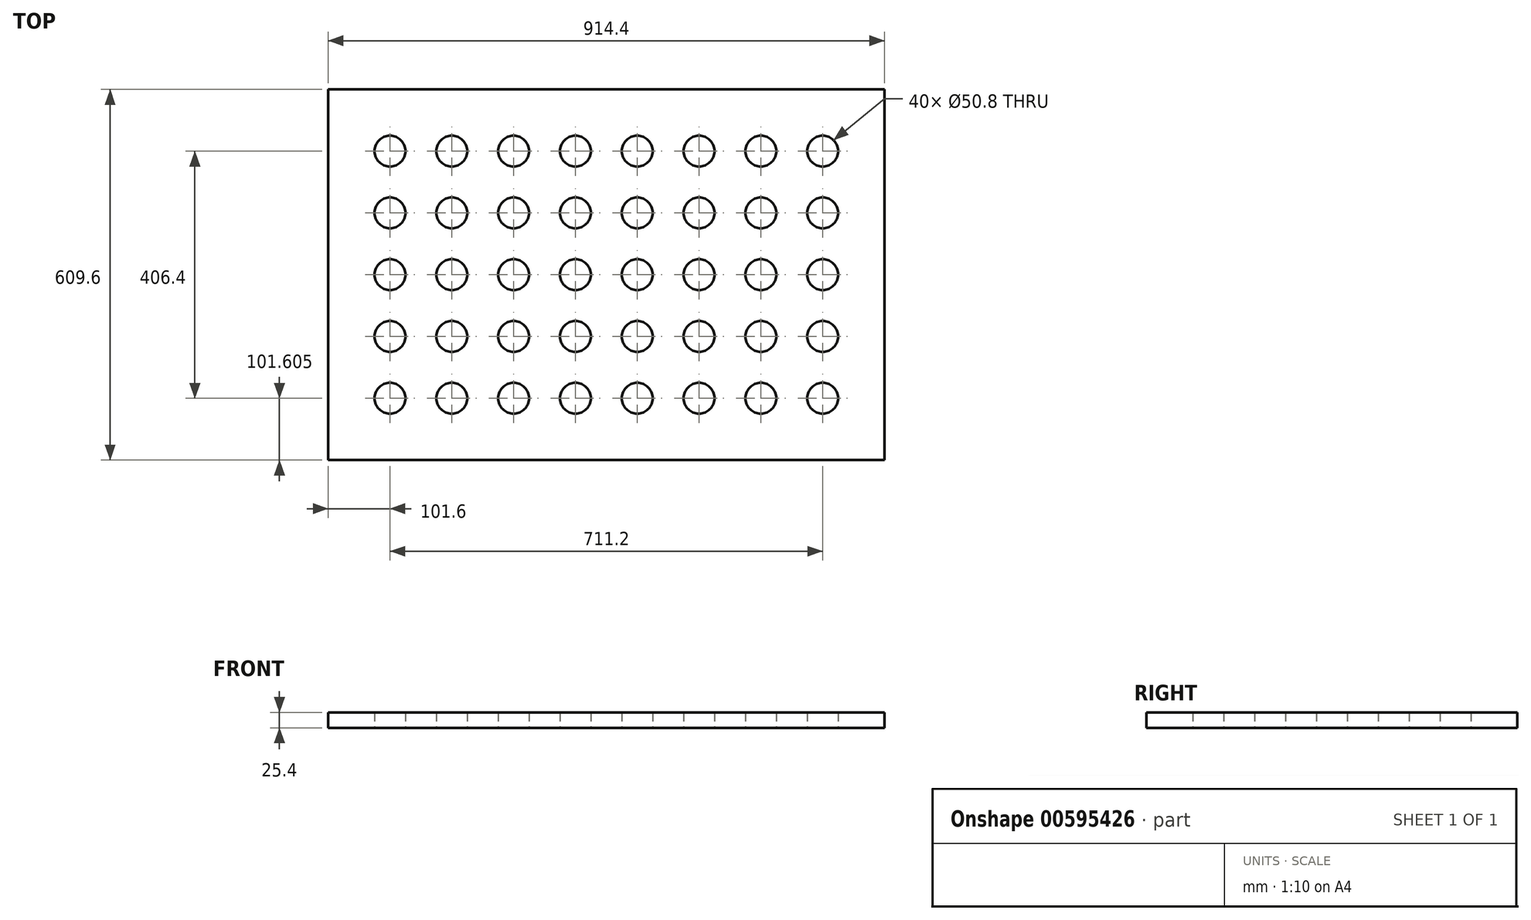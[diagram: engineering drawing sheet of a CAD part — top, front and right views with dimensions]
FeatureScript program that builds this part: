
annotation { "Feature Type Name" : "Feature", "Feature Type Description" : "" }
export const myFeature = defineFeature(function(context is Context, id is Id, definition is map)
    precondition{}
    {
        {
            var Q0;
            Q0=qCreatedBy(makeId("Top.planeOp"),FACE);
            var sketch = newSketch(context, id + "F0", { "sketchPlane" : qUnion([Q0])});
            skLineSegment(sketch, "E0.bottom", {"start": v(812.8, 482.96) * mm, "end": v(-101.6, 482.96) * mm});
            skLineSegment(sketch, "E0.top", {"start": v(812.8, -126.64) * mm, "end": v(-101.6, -126.64) * mm});
            skLineSegment(sketch, "E0.left", {"start": v(812.8, 482.96) * mm, "end": v(812.8, -126.64) * mm});
            skLineSegment(sketch, "E0.right", {"start": v(-101.6, 482.96) * mm, "end": v(-101.6, -126.64) * mm});
            skCircle(sketch, "E1", {"center": v(0, 381.36) * mm, "radius": 25.4 * mm});
            skCircle(sketch, "E2", {"center": v(101.6, 381.36) * mm, "radius": 25.4 * mm});
            skCircle(sketch, "E3", {"center": v(203.2, 381.36) * mm, "radius": 25.4 * mm});
            skCircle(sketch, "E4", {"center": v(304.8, 381.36) * mm, "radius": 25.4 * mm});
            skCircle(sketch, "E5", {"center": v(406.4, 381.36) * mm, "radius": 25.4 * mm});
            skCircle(sketch, "E6", {"center": v(508, 381.36) * mm, "radius": 25.4 * mm});
            skCircle(sketch, "E7", {"center": v(609.6, 381.36) * mm, "radius": 25.4 * mm});
            skCircle(sketch, "E8", {"center": v(711.2, 381.36) * mm, "radius": 25.4 * mm});
            skCircle(sketch, "E9", {"center": v(0, 279.76) * mm, "radius": 25.4 * mm});
            skCircle(sketch, "E10", {"center": v(0, 178.16) * mm, "radius": 25.4 * mm});
            skCircle(sketch, "E11", {"center": v(0, 76.56) * mm, "radius": 25.4 * mm});
            skCircle(sketch, "E12", {"center": v(0, -25.04) * mm, "radius": 25.4 * mm});
            skCircle(sketch, "E13", {"center": v(101.6, 279.76) * mm, "radius": 25.4 * mm});
            skCircle(sketch, "E14", {"center": v(101.6, 178.16) * mm, "radius": 25.4 * mm});
            skCircle(sketch, "E15", {"center": v(101.6, 76.56) * mm, "radius": 25.4 * mm});
            skCircle(sketch, "E16", {"center": v(101.6, -25.04) * mm, "radius": 25.4 * mm});
            skCircle(sketch, "E17", {"center": v(203.2, 279.76) * mm, "radius": 25.4 * mm});
            skCircle(sketch, "E18", {"center": v(304.8, 279.76) * mm, "radius": 25.4 * mm});
            skCircle(sketch, "E19", {"center": v(406.4, 279.76) * mm, "radius": 25.4 * mm});
            skCircle(sketch, "E20", {"center": v(508, 279.76) * mm, "radius": 25.4 * mm});
            skCircle(sketch, "E21", {"center": v(609.6, 279.76) * mm, "radius": 25.4 * mm});
            skCircle(sketch, "E22", {"center": v(711.2, 279.76) * mm, "radius": 25.4 * mm});
            skCircle(sketch, "E23", {"center": v(203.2, 178.16) * mm, "radius": 25.4 * mm});
            skCircle(sketch, "E24", {"center": v(304.8, 178.16) * mm, "radius": 25.4 * mm});
            skCircle(sketch, "E25", {"center": v(406.4, 178.16) * mm, "radius": 25.4 * mm});
            skCircle(sketch, "E26", {"center": v(508, 178.16) * mm, "radius": 25.4 * mm});
            skCircle(sketch, "E27", {"center": v(609.6, 178.16) * mm, "radius": 25.4 * mm});
            skCircle(sketch, "E28", {"center": v(711.2, 178.16) * mm, "radius": 25.4 * mm});
            skCircle(sketch, "E29", {"center": v(203.2, 76.56) * mm, "radius": 25.4 * mm});
            skCircle(sketch, "E30", {"center": v(406.4, 76.56) * mm, "radius": 25.4 * mm});
            skCircle(sketch, "E31", {"center": v(508, 76.56) * mm, "radius": 25.4 * mm});
            skCircle(sketch, "E32", {"center": v(609.6, 76.56) * mm, "radius": 25.4 * mm});
            skCircle(sketch, "E33", {"center": v(711.2, 76.56) * mm, "radius": 25.4 * mm});
            skCircle(sketch, "E34", {"center": v(203.2, -25.04) * mm, "radius": 25.4 * mm});
            skCircle(sketch, "E35", {"center": v(406.4, -25.04) * mm, "radius": 25.4 * mm});
            skCircle(sketch, "E36", {"center": v(508, -25.04) * mm, "radius": 25.4 * mm});
            skCircle(sketch, "E37", {"center": v(609.6, -25.04) * mm, "radius": 25.4 * mm});
            skCircle(sketch, "E38", {"center": v(711.2, -25.04) * mm, "radius": 25.4 * mm});
            skCircle(sketch, "E39", {"center": v(304.8, 76.56) * mm, "radius": 25.4 * mm});
            skCircle(sketch, "E40", {"center": v(304.8, -25.04) * mm, "radius": 25.4 * mm});
            skSolve(sketch);
        }
        {
            var Q0;
            Q0=makeQuery(id+"F0.imprint","IMPRINT",FACE,{"disambiguationData":[TD([[makeQuery(id+"F0.imprint","IMPRINT",EDGE,{"derivedFrom":sQuery(id+"F0.wireOp",EDGE,"E0.bottom")}),1.0]])]});
            extrude(context, id + "F1", {"entities" : qUnion([Q0]), "depth" : 25.4 * mm, "offsetDistance" : 25.4 * mm});
        }
    });
